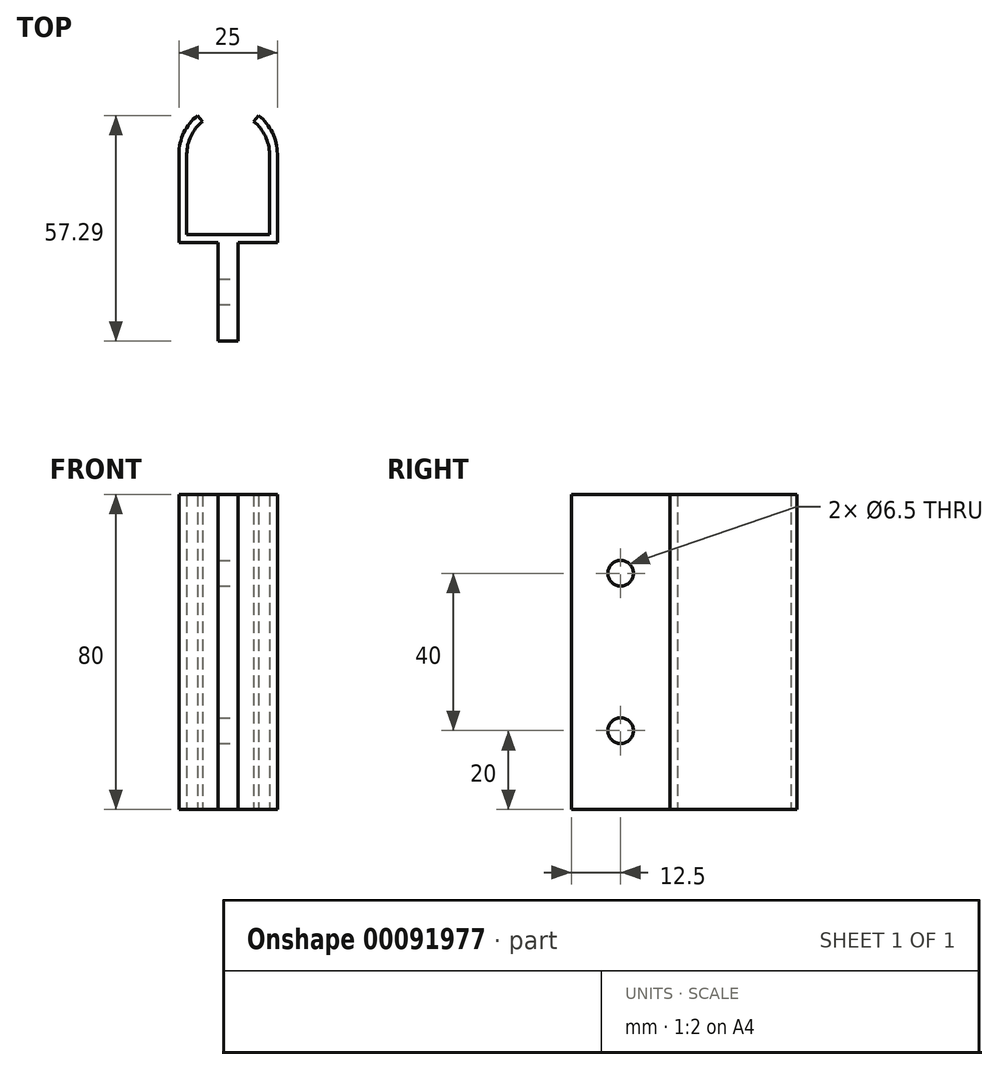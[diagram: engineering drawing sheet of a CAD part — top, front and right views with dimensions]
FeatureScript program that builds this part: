
annotation { "Feature Type Name" : "Feature", "Feature Type Description" : "" }
export const myFeature = defineFeature(function(context is Context, id is Id, definition is map)
    precondition{}
    {
        {
            var Q0;
            Q0=qCreatedBy(makeId("Top.planeOp"),FACE);
            var sketch = newSketch(context, id + "F0", { "sketchPlane" : qUnion([Q0])});
            skLineSegment(sketch, "E0.bottom", {"start": v(12.5, -11.25) * mm, "end": v(-12.5, -11.25) * mm});
            skLineSegment(sketch, "E0.top", {"start": v(12.5, 11.25) * mm, "end": v(-12.5, 11.25) * mm, "construction": true});
            skLineSegment(sketch, "E0.left", {"start": v(12.5, -11.25) * mm, "end": v(12.5, 11.25) * mm, "construction": true});
            skLineSegment(sketch, "E0.right", {"start": v(-12.5, -11.25) * mm, "end": v(-12.5, 11.25) * mm, "construction": true});
            skPoint(sketch, "E0.middle", {"position": v(0, 0) * mm});
            skCircle(sketch, "E1", {"center": v(0, 11.25) * mm, "radius": 12.5 * mm, "construction": true});
            skArc(sketch, "E2", {"start": v(-12.5, 11.25) * mm, "mid": v(-11.26, 16.68) * mm, "end": v(-7.78, 21.04) * mm});
            skArc(sketch, "E3", {"start": v(12.5, 11.25) * mm, "mid": v(11.26, 16.68) * mm, "end": v(7.78, 21.04) * mm});
            skLineSegment(sketch, "E4", {"start": v(-12.5, 11.25) * mm, "end": v(-12.5, -11.25) * mm});
            skLineSegment(sketch, "E5", {"start": v(12.5, -11.25) * mm, "end": v(12.5, 11.25) * mm});
            skArc(sketch, "E6.0", {"start": v(-10.5, 11.25) * mm, "mid": v(-9.46, 15.81) * mm, "end": v(-6.53, 19.47) * mm});
            skArc(sketch, "E6.1", {"start": v(10.5, 11.25) * mm, "mid": v(9.46, 15.81) * mm, "end": v(6.53, 19.47) * mm});
            skLineSegment(sketch, "E6.2", {"start": v(10.5, -9.25) * mm, "end": v(10.5, 11.25) * mm});
            skLineSegment(sketch, "E6.3", {"start": v(10.5, -9.25) * mm, "end": v(-10.5, -9.25) * mm});
            skLineSegment(sketch, "E6.4", {"start": v(-10.5, 11.25) * mm, "end": v(-10.5, -9.25) * mm});
            skLineSegment(sketch, "E7", {"start": v(-7.78, 21.04) * mm, "end": v(-6.53, 19.47) * mm});
            skLineSegment(sketch, "E8", {"start": v(7.78, 21.04) * mm, "end": v(6.53, 19.47) * mm});
            skSolve(sketch);
        }
        {
            var Q0;
            Q0=qCreatedBy(makeId("Top.planeOp"),FACE);
            var sketch = newSketch(context, id + "F1", { "sketchPlane" : qUnion([Q0])});
            skLineSegment(sketch, "E9.0", {"start": v(12.5, -11.25) * mm, "end": v(-12.5, -11.25) * mm, "construction": true});
            skLineSegment(sketch, "E10.bottom", {"start": v(2.5, -36.25) * mm, "end": v(-2.5, -36.25) * mm});
            skLineSegment(sketch, "E10.top", {"start": v(2.5, 13.75) * mm, "end": v(-2.5, 13.75) * mm, "construction": true});
            skLineSegment(sketch, "E10.left", {"start": v(2.5, -36.25) * mm, "end": v(2.5, 13.75) * mm, "construction": true});
            skLineSegment(sketch, "E10.right", {"start": v(-2.5, -36.25) * mm, "end": v(-2.5, 13.75) * mm, "construction": true});
            skPoint(sketch, "E10.middle", {"position": v(0, -11.25) * mm});
            skLineSegment(sketch, "E11.bottom", {"start": v(-2.5, -11.25) * mm, "end": v(2.5, -11.25) * mm});
            skLineSegment(sketch, "E11.top", {"start": v(-2.5, -36.25) * mm, "end": v(2.5, -36.25) * mm});
            skLineSegment(sketch, "E11.left", {"start": v(-2.5, -11.25) * mm, "end": v(-2.5, -36.25) * mm});
            skLineSegment(sketch, "E11.right", {"start": v(2.5, -11.25) * mm, "end": v(2.5, -36.25) * mm});
            skSolve(sketch);
        }
        {
            var Q0;
            Q0=makeQuery(id+"F0.imprint","IMPRINT",FACE,{"disambiguationData":[TD([[makeQuery(id+"F0.imprint","IMPRINT",EDGE,{"derivedFrom":sQuery(id+"F0.wireOp",EDGE,"E0.bottom")}),-1.0]])]});
            extrude(context, id + "F2", {"entities" : qUnion([Q0]), "depth" : 80 * mm});
        }
        {
            var Q0;
            Q0=makeQuery(id+"F1.imprint","IMPRINT",FACE,{"disambiguationData":[TD([[makeQuery(id+"F1.imprint","IMPRINT",EDGE,{"derivedFrom":sQuery(id+"F1.wireOp",EDGE,"E11.bottom")}),-1.0]])]});
            extrude(context, id + "F3", {"entities" : qUnion([Q0]), "operationType" : NewBodyOperationType.ADD, "depth" : 80 * mm});
        }
        {
            var Q0;
            Q0=qCreatedBy(makeId("Right.planeOp"),FACE);
            var sketch = newSketch(context, id + "F4", { "sketchPlane" : qUnion([Q0])});
            skPoint(sketch, "E12.0", {"position": v(-36.25, 0) * mm});
            skLineSegment(sketch, "E13.bottom", {"start": v(-36.25, 0) * mm, "end": v(-23.75, 0) * mm, "construction": true});
            skLineSegment(sketch, "E13.top", {"start": v(-36.25, 20) * mm, "end": v(-23.75, 20) * mm, "construction": true});
            skLineSegment(sketch, "E13.left", {"start": v(-36.25, 0) * mm, "end": v(-36.25, 20) * mm, "construction": true});
            skLineSegment(sketch, "E13.right", {"start": v(-23.75, 0) * mm, "end": v(-23.75, 20) * mm, "construction": true});
            skCircle(sketch, "E14", {"center": v(-23.75, 20) * mm, "radius": 3.25 * mm});
            skCircle(sketch, "E15.0.1.0", {"center": v(-23.75, 60) * mm, "radius": 3.25 * mm});
            skLineSegment(sketch, "E15.direction1", {"start": v(-23.75, 20) * mm, "end": v(-6.25, 20) * mm, "construction": true});
            skLineSegment(sketch, "E15.direction2", {"start": v(-23.75, 20) * mm, "end": v(-23.75, 60) * mm, "construction": true});
            skSolve(sketch);
        }
        {
            var Q0;
            Q0 = qSketchRegion(id + "F4", true);
            extrude(context, id + "F5", {"entities" : qUnion([Q0]), "operationType" : NewBodyOperationType.REMOVE, "oppositeDirection" : true, "depth" : 25 * mm, "hasSecondDirection" : true, "secondDirectionOppositeDirection" : false, "secondDirectionDepth" : 25 * mm});
        }
    });
